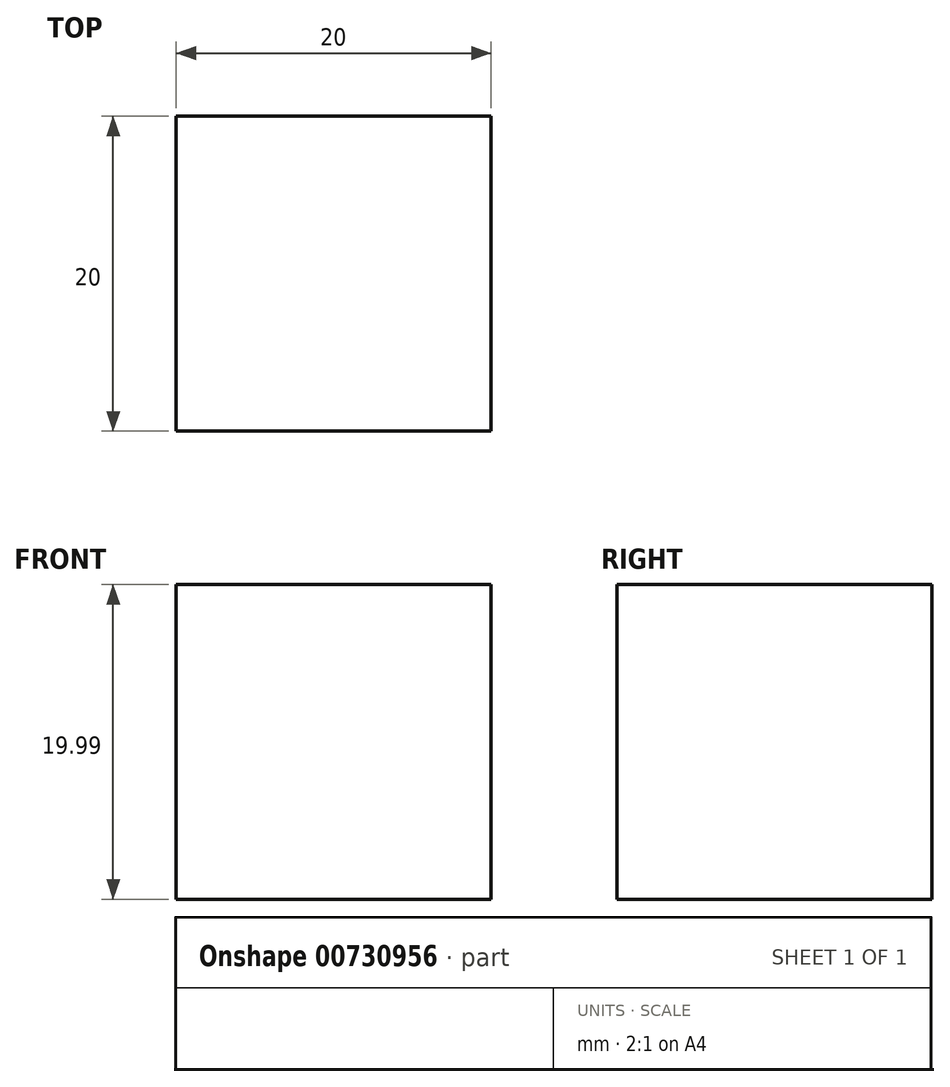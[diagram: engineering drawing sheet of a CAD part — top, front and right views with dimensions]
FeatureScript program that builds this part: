
annotation { "Feature Type Name" : "Feature", "Feature Type Description" : "" }
export const myFeature = defineFeature(function(context is Context, id is Id, definition is map)
    precondition{}
    {
        {
            var Q0;
            Q0=qCreatedBy(makeId("Top.planeOp"),FACE);
            var sketch = newSketch(context, id + "F0", { "sketchPlane" : qUnion([Q0])});
            skLineSegment(sketch, "E0.bottom", {"start": v(0, -2.78) * mm, "end": v(-20, -2.78) * mm});
            skLineSegment(sketch, "E0.top", {"start": v(0, 17.22) * mm, "end": v(-20, 17.22) * mm});
            skLineSegment(sketch, "E0.left", {"start": v(0, -2.78) * mm, "end": v(0, 17.22) * mm});
            skLineSegment(sketch, "E0.right", {"start": v(-20, -2.78) * mm, "end": v(-20, 17.22) * mm});
            skPoint(sketch, "E0.middle", {"position": v(-10, 7.22) * mm});
            skSolve(sketch);
        }
        {
            var Q0;
            Q0 = qSketchRegion(id + "F0", true);
            extrude(context, id + "F1", {"entities" : qUnion([Q0]), "depth" : 19.99 * mm, "offsetDistance" : 25.4 * mm});
        }
        {
            var Q0;
            Q0=makeQuery(id+"F1.opExtrude","CAP_FACE",FACE,{"disambiguationData":[OSD([sQuery(id+"F0.wireOp",EDGE,"E0.bottom"),sQuery(id+"F0.wireOp",EDGE,"E0.top"),sQuery(id+"F0.wireOp",EDGE,"E0.left"),sQuery(id+"F0.wireOp",EDGE,"E0.right")])],"isStart":false});
            var sketch = newSketch(context, id + "F2", { "sketchPlane" : qUnion([Q0])});
            skLineSegment(sketch, "E1.bottom", {"start": v(-18.3, 5) * mm, "end": v(-13.3, 5) * mm});
            skLineSegment(sketch, "E1.top", {"start": v(-18.3, 0) * mm, "end": v(-13.3, 0) * mm});
            skLineSegment(sketch, "E1.left", {"start": v(-18.3, 5) * mm, "end": v(-18.3, 0) * mm});
            skLineSegment(sketch, "E1.right", {"start": v(-13.3, 5) * mm, "end": v(-13.3, 0) * mm});
            skLineSegment(sketch, "E2", {"start": v(-10, 17.22) * mm, "end": v(-10, -2.78) * mm});
            skLineSegment(sketch, "E3.MirrorCS", {"start": v(-6.7, 5) * mm, "end": v(-6.7, 0) * mm});
            skLineSegment(sketch, "E4.MirrorCS", {"start": v(-1.7, 5) * mm, "end": v(-6.7, 5) * mm});
            skLineSegment(sketch, "E5.MirrorCS", {"start": v(-1.7, 0) * mm, "end": v(-6.7, 0) * mm});
            skLineSegment(sketch, "E6.MirrorCS", {"start": v(-1.7, 5) * mm, "end": v(-1.7, 0) * mm});
            skSolve(sketch);
        }
        {
            var Q0;
            Q0=makeQuery(id+"F2.imprint","IMPRINT",FACE,{"disambiguationData":[TD([[makeQuery(id+"F2.imprint","IMPRINT",EDGE,{"derivedFrom":sQuery(id+"F2.wireOp",EDGE,"E1.bottom")}),-1.0]])]});
            var Q1;
            Q1 = qSketchRegion(id + "F2", true);
            var Q2;
            Q2=makeQuery(id+"F2.imprint","IMPRINT",FACE,{"disambiguationData":[TD([[makeQuery(id+"F2.imprint","IMPRINT",EDGE,{"derivedFrom":sQuery(id+"F2.wireOp",EDGE,"E3.MirrorCS")}),1.0]])]});
            extrude(context, id + "F3", {"entities" : qUnion([Q0, Q1, Q2]), "operationType" : NewBodyOperationType.ADD, "oppositeDirection" : true, "depth" : 3 * mm, "offsetDistance" : 25.4 * mm});
        }
    });
